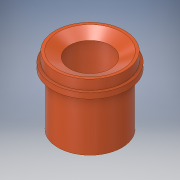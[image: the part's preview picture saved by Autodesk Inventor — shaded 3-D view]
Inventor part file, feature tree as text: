
AUTODESK INVENTOR PART (.ipt)
format: ipt  version: 2017 (Build 210142000, 142)  size: 169,984 bytes
history: native  units: in
note: dims shown in document units (in); Inventor stores cm internally (conversion verified against a paired STEP export)
features: revolve x1, sketch x1
ambient origin geometry x8: Origin, YZ Plane, XZ Plane, XY Plane, X Axis, Y Axis, Z Axis, Center Point
bodies: Body1 (feature_tree)
feature tree (2):
  revolve  "Revolution2"  [1 undecoded]
  sketch  "Sketch1"  dims[d0=1.13in d1=3.4in d2=0.25in d3=0.1718in d5=1.0in d6=1.0in d7=90.0deg d8=0.5in d9=15.0deg d11=0.25in d12=1.25in d13=0.25in d15=0.25in d16=0.5in d17=0.5in d18=0.5in d19=2.5in d20=0.5in d22=0.375in d23=0.25in d25=0.234in d26=15.0deg d28=90.0deg]
note: 1 required parameter value undecoded (feature->parameter linkage not recoverable at this tier; creation-order binding heuristic only, values carry confidence <= 0.55)
